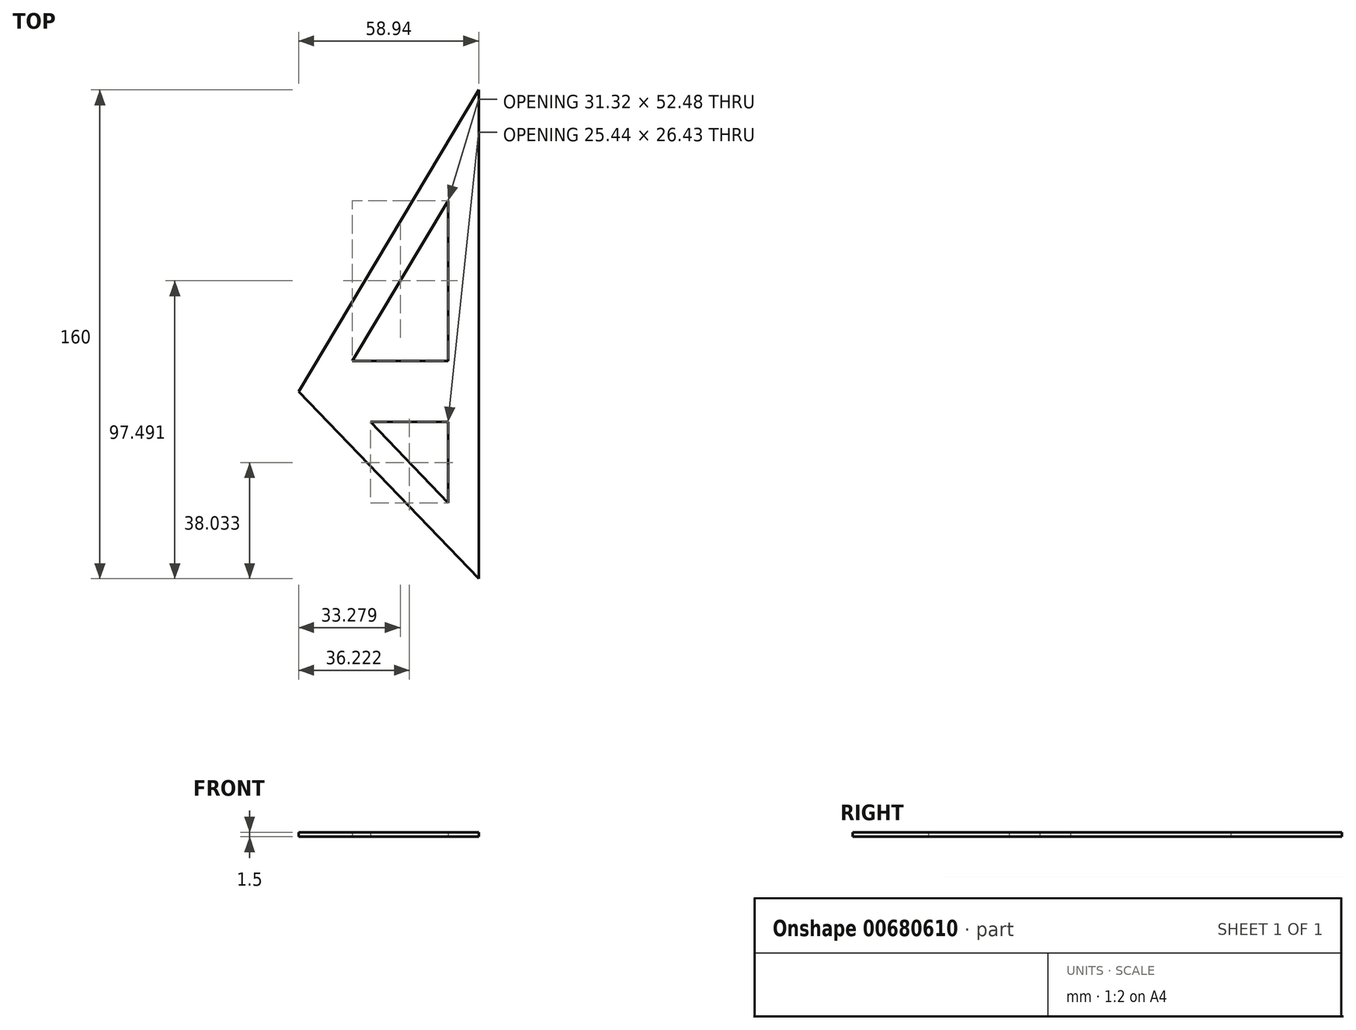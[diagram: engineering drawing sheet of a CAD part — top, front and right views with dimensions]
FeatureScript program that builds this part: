
annotation { "Feature Type Name" : "Feature", "Feature Type Description" : "" }
export const myFeature = defineFeature(function(context is Context, id is Id, definition is map)
    precondition{}
    {
        {
            var Q0;
            Q0=qCreatedBy(makeId("Top.planeOp"),FACE);
            var sketch = newSketch(context, id + "F0", { "sketchPlane" : qUnion([Q0])});
            skLineSegment(sketch, "E0", {"start": v(0, -61.25) * mm, "end": v(0, 98.75) * mm});
            skLineSegment(sketch, "E1", {"start": v(0, 98.75) * mm, "end": v(-58.94, 0) * mm});
            skLineSegment(sketch, "E2", {"start": v(-58.94, 0) * mm, "end": v(0, -61.25) * mm});
            skLineSegment(sketch, "E3", {"start": v(-58.94, 0) * mm, "end": v(0, 0) * mm});
            skLineSegment(sketch, "E4.0", {"start": v(-41.32, 10) * mm, "end": v(-10, 10) * mm});
            skLineSegment(sketch, "E5.0", {"start": v(-35.44, -10) * mm, "end": v(-10, -10) * mm});
            skLineSegment(sketch, "E5.1", {"start": v(-35.44, -10) * mm, "end": v(-10, -36.43) * mm});
            skLineSegment(sketch, "E6.trimOffspring", {"start": v(-10, 62.48) * mm, "end": v(-41.32, 10) * mm});
            skLineSegment(sketch, "E7.trimOffspring", {"start": v(-10, 10) * mm, "end": v(-10, 62.48) * mm});
            skLineSegment(sketch, "E8.trimOffspring", {"start": v(-10, -36.43) * mm, "end": v(-10, -10) * mm});
            skSolve(sketch);
        }
        {
            var Q0;
            Q0 = qSketchRegion(id + "F0", true);
            extrude(context, id + "F1", {"entities" : qUnion([Q0]), "depth" : 1.5 * mm, "offsetDistance" : 25 * mm});
        }
    });
